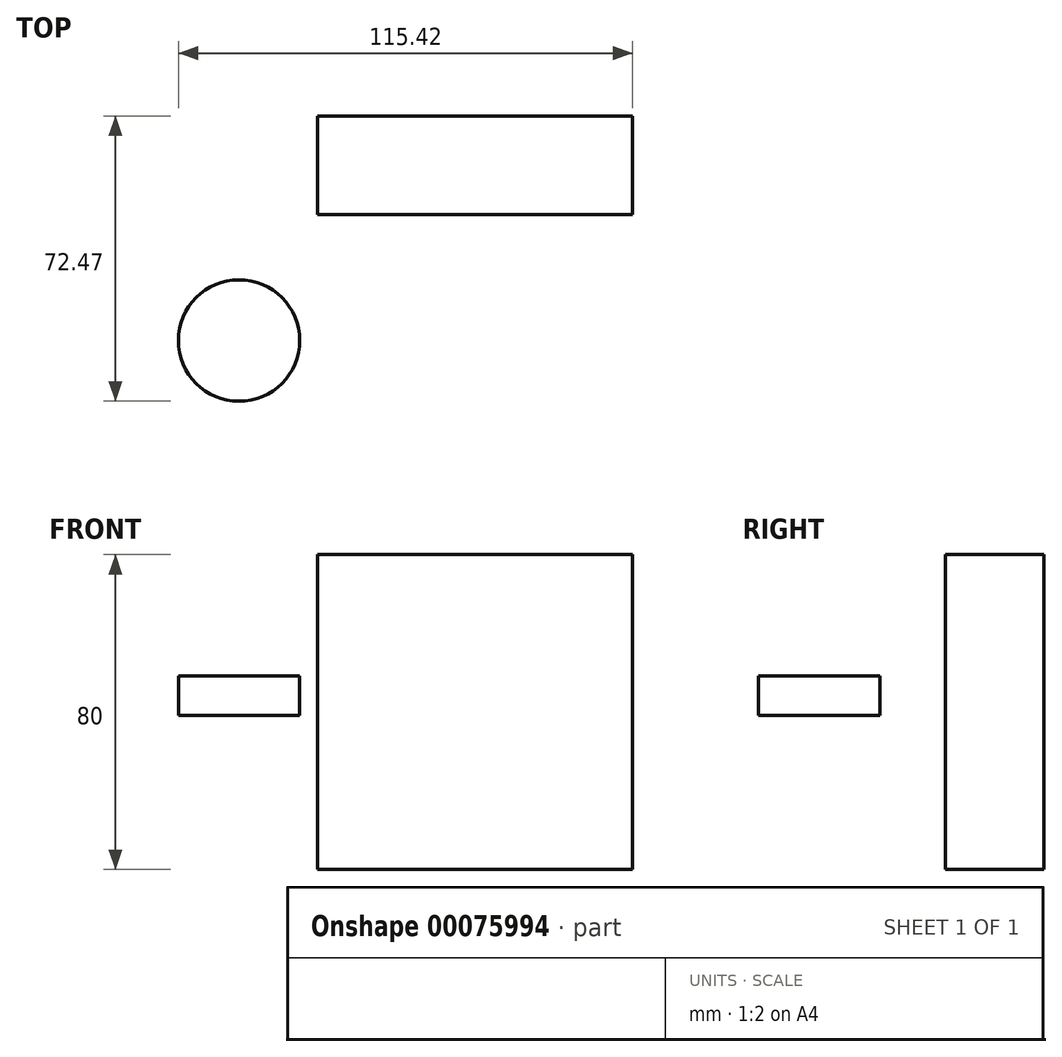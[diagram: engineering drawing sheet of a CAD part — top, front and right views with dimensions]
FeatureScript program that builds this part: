
annotation { "Feature Type Name" : "Feature", "Feature Type Description" : "" }
export const myFeature = defineFeature(function(context is Context, id is Id, definition is map)
    precondition{}
    {
        {
            var Q0;
            Q0=qCreatedBy(makeId("Front.planeOp"),FACE);
            var sketch = newSketch(context, id + "F0", { "sketchPlane" : qUnion([Q0])});
            skLineSegment(sketch, "E0.bottom", {"start": v(-37.94, 40.78) * mm, "end": v(42.06, 40.78) * mm});
            skLineSegment(sketch, "E0.top", {"start": v(-37.94, -39.22) * mm, "end": v(42.06, -39.22) * mm});
            skLineSegment(sketch, "E0.left", {"start": v(-37.94, 40.78) * mm, "end": v(-37.94, -39.22) * mm});
            skLineSegment(sketch, "E0.right", {"start": v(42.06, 40.78) * mm, "end": v(42.06, -39.22) * mm});
            skSolve(sketch);
        }
        {
            var Q0;
            Q0=makeQuery(id+"F0.imprint","IMPRINT",FACE,{"disambiguationData":[TD([[makeQuery(id+"F0.imprint","IMPRINT",EDGE,{"derivedFrom":sQuery(id+"F0.wireOp",EDGE,"E0.bottom")}),-1.0]])]});
            extrude(context, id + "F1", {"entities" : qUnion([Q0]), "depth" : 25 * mm});
        }
        {
            var Q0;
            Q0=qCreatedBy(makeId("Top.planeOp"),FACE);
            var sketch = newSketch(context, id + "F2", { "sketchPlane" : qUnion([Q0])});
            skCircle(sketch, "E1", {"center": v(-57.95, -57.06) * mm, "radius": 15.41 * mm});
            skSolve(sketch);
        }
        {
            var Q0;
            Q0=makeQuery(id+"F2.imprint","IMPRINT",FACE,{"disambiguationData":[TD([[makeQuery(id+"F2.imprint","IMPRINT",EDGE,{"derivedFrom":sQuery(id+"F2.wireOp",EDGE,"E1")}),1.0]])]});
            extrude(context, id + "F3", {"entities" : qUnion([Q0]), "depth" : 10 * mm});
        }
    });
